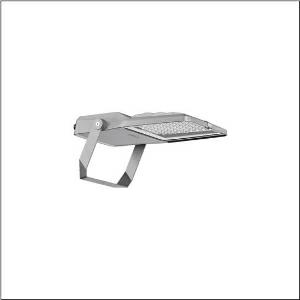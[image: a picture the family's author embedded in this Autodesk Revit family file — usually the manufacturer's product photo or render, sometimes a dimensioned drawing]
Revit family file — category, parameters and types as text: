
# Revit family: floodlight_fl_21_iq_mini___pl43_5xa7771d2a1a_9b6a
name_source: partatom
category: Lighting Fixtures
units: mm (PartAtom-declared; Revit-internal decimal feet)

## family parameters
Cut with Voids When Loaded = No
Host = Face
Light Source = No
Part Type = Normal
Room Calculation Point = No
Round Connector Dimension = Use Diameter
Shared = No

## types (1)
- --- (1 x LED, 18290 lm, 143 W, 3000K)
    Apparent Load = 143 VA
    CIE Flux Codes = 27 78 99 100 100
    Color Rendering = 70
    Color Temperature = 3000K
    Default Elevation = 1800 mm
    Description = Floodlight FL 21 iQ mini, floodlight, primary light control with lens, of PMMA, primary optical cover: protective disc, of toughened safety glass, transparent, light distribution: PL43, light emission: direct distribution, installation type: surface-mounted, LED, High Power LED, rated luminous flux: 18.290lm, luminous efficacy: 128lm/W, light colour: 730, colour temperature: 3000K, control gear: iQ Comfort/DALI, control: Auto-Match, Temp-Guard, Lumen-Switch, Night-Set, Smart-Wire, Light-Fading, Desk-Remote (wireless, voltage-free reading and setting of iQ features in the workshop via application-optimized NFC function/RFID function), optimised constant luminous flux control (CLO 2.0), with terminal, 6-pole, mains connection: 220..240V, AC, 50/60Hz, start of lifetime: 143W, end of service life: 152W, reduction: 61W, luminaire housing, of diecast aluminium, powder-coated, Siteco® metallic grey (DB 702S), corrosivity category C5 mid according to DIN EN ISO 12944, suitable for swimming pools, chlorine-resistant, sealing non-destructively replaceable, mounting bracket, of steel, galvanised, powder-coated, Siteco® metallic grey (DB 702S), protection rating (complete): IP66, insulation class (complete): insulation class II (safety insulation), certification: CE, ENEC, VDE, protection symbol: D, impact resistance: IK08, permissible operating ambient temperature: -40..+40°C, permissible operating ambient temperature for outdoor applications: -40..+50°C, standard: DIN EN 12944, LABS conformity tested according to VDMA 24364:2018-05, packaging unit: 1 piece

Light Distribution: PL43
    Height = 70 mm
    Lamp = 1 x LED
    Lamp Light Flux = 18290 lm
    Lamp Power = 143 W
    Lamp count = 1
    Length = 485 mm
    Luminous efficacy = 128 lm/W
    Manufacturer = Siteco
    ModVariant = No
    Model = 5XA7771D2A1A
    Number of Poles = 1
    OnlyDefault = Yes
    Power Factor = 1
    Product Name = Floodlight FL 21 iQ mini | PL43
    Product group = floodlight | pylon annexe
    ProductGroupID = 6200
    Protection Class = Protection class II
    Protection Degree = IP 66
    RLX_Detail_Level = 1
    RLX_Emergency_Light_Flux = 0 lm
    RLX_Emergency_Type = 0
    RLX_Emergency_Type_DB = No
    RlxData = <blob elided: 96521 chars, md5=51adefdd>
    Socket = socket
    Standby Power = 0 W
    System Light Flux = 18290 lm
    System Power = 143 W
    Type Comments = factory setting: luminous flux: 100 % | dim-lin: 254 | 730 mA
    Type Image = l_1006845.jpg
    URL = http://relux.com
    VarID = @adj_162088
    Voltage = 0 V
    Weight = 0.00 kg
    Width = 337 mm

## geometry (parser evidence)
native form markers: Blend x4, Sweep x12
no freeform markers — native parametric forms only
